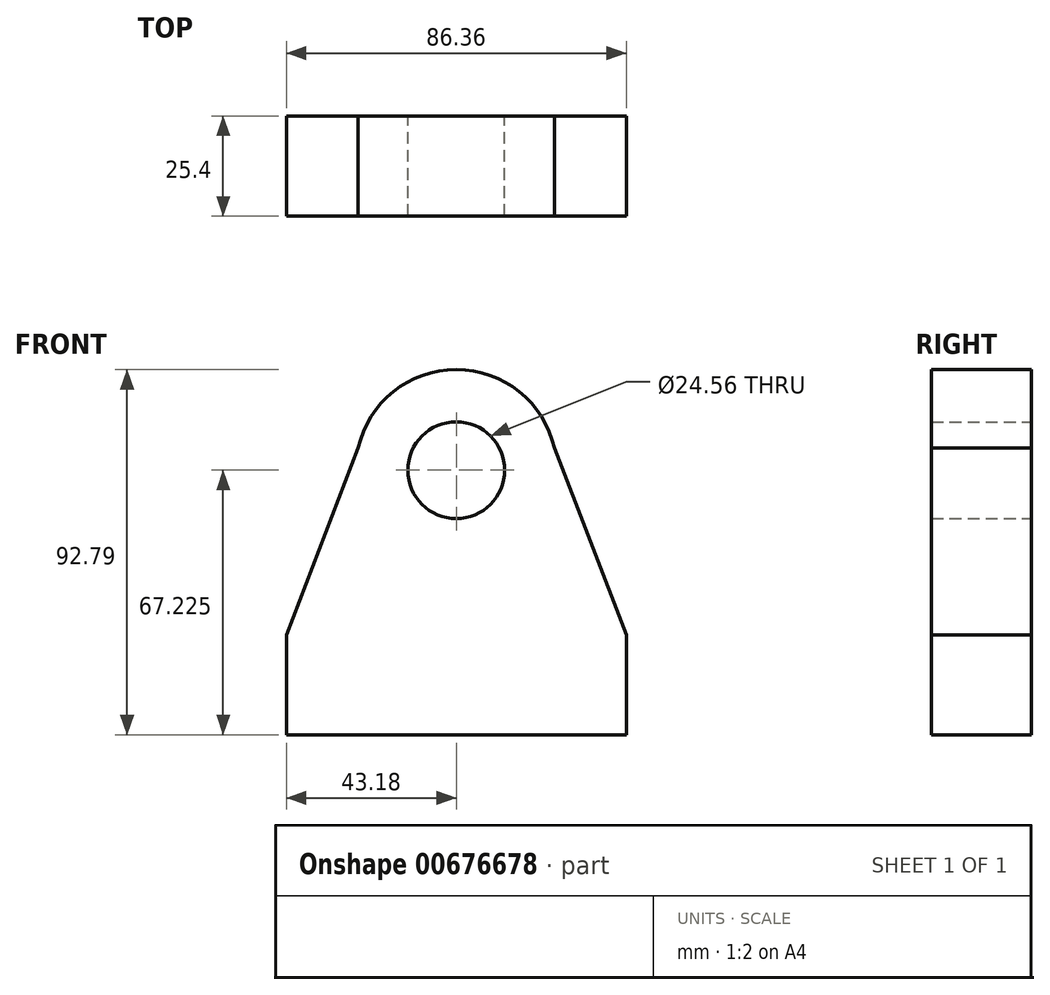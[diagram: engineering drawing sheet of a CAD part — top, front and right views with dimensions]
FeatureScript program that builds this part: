
annotation { "Feature Type Name" : "Feature", "Feature Type Description" : "" }
export const myFeature = defineFeature(function(context is Context, id is Id, definition is map)
    precondition{}
    {
        {
            var Q0;
            Q0=qCreatedBy(makeId("Front.planeOp"),FACE);
            var sketch = newSketch(context, id + "F0", { "sketchPlane" : qUnion([Q0])});
            skCircle(sketch, "E0", {"center": v(0, 25.57) * mm, "radius": 25.57 * mm});
            skPoint(sketch, "E0.first.point", {"position": v(0, 0) * mm});
            skPoint(sketch, "E0.second.point", {"position": v(0, 51.13) * mm});
            skPoint(sketch, "E0.third.point", {"position": v(-24.95, 31.15) * mm});
            skLineSegment(sketch, "E1.bottom", {"start": v(-43.18, -16.26) * mm, "end": v(43.18, -16.26) * mm});
            skLineSegment(sketch, "E1.top", {"start": v(-43.18, -41.66) * mm, "end": v(43.18, -41.66) * mm});
            skLineSegment(sketch, "E1.left", {"start": v(-43.18, -16.26) * mm, "end": v(-43.18, -41.66) * mm});
            skLineSegment(sketch, "E1.right", {"start": v(43.18, -16.26) * mm, "end": v(43.18, -41.66) * mm});
            skLineSegment(sketch, "E2", {"start": v(-24.95, 31.15) * mm, "end": v(-43.18, -16.26) * mm});
            skLineSegment(sketch, "E3", {"start": v(24.95, 31.15) * mm, "end": v(43.18, -16.26) * mm});
            skCircle(sketch, "E4", {"center": v(0, 25.57) * mm, "radius": 12.28 * mm});
            skSolve(sketch);
        }
        {
            var Q0;
            Q0=makeQuery(id+"F0.imprint","IMPRINT",FACE,{"disambiguationData":[TD([[makeQuery(id+"F0.imprint","IMPRINT",EDGE,{"derivedFrom":sQuery(id+"F0.wireOp",EDGE,"E1.bottom")}),1.0]])]});
            var Q1;
            Q1=makeQuery(id+"F0.imprint","IMPRINT",FACE,{"disambiguationData":[TD([[makeQuery(id+"F0.imprint","IMPRINT",EDGE,{"derivedFrom":sQuery(id+"F0.wireOp",EDGE,"E1.bottom")}),-1.0]])]});
            var Q2;
            {var subQ0=sQuery(id+"F0.wireOp",EDGE,"E0");var subQ1=makeQuery(id+"F0.imprint","INTERSECT",VERTEX,{"derivedFrom":[subQ0,sQuery(id+"F0.wireOp",EDGE,"E2")]});Q2=makeQuery(id+"F0.imprint","IMPRINT",FACE,{"disambiguationData":[TD([[makeQuery(id+"F0.imprint","IMPRINT",EDGE,{"disambiguationData":[TD([[subQ1,1.0]])],"derivedFrom":subQ0}),1.0]])]});}
            extrude(context, id + "F1", {"entities" : qUnion([Q0, Q1, Q2]), "depth" : 25.4 * mm, "offsetDistance" : 25.4 * mm});
        }
    });
